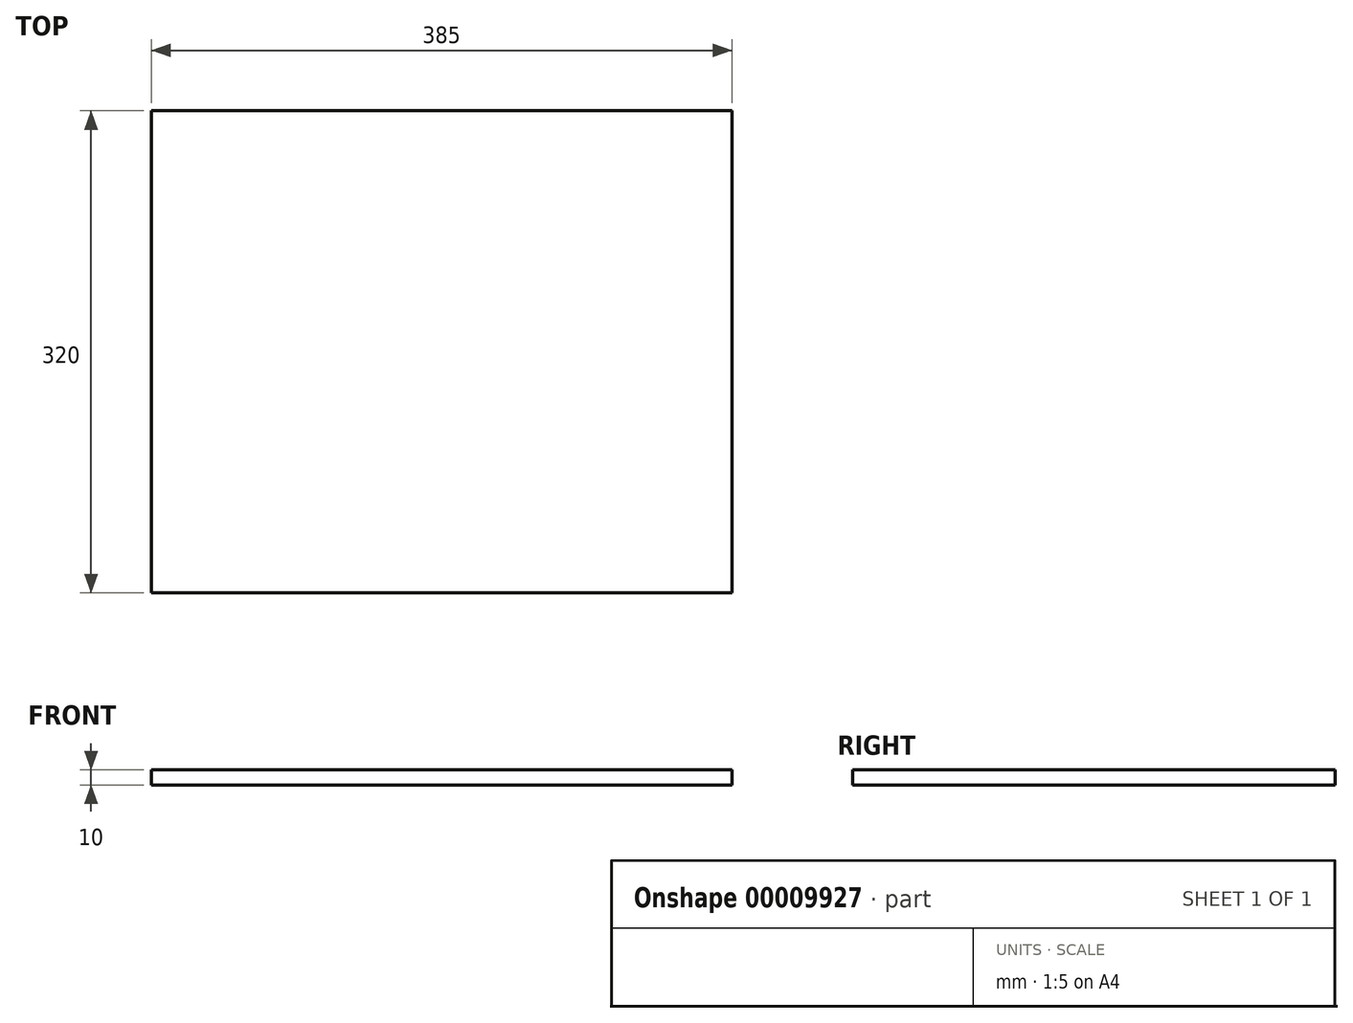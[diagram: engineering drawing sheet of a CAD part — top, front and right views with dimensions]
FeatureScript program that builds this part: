
annotation { "Feature Type Name" : "Feature", "Feature Type Description" : "" }
export const myFeature = defineFeature(function(context is Context, id is Id, definition is map)
    precondition{}
    {
        {
            var Q0;
            Q0=qCreatedBy(makeId("Top.planeOp"),FACE);
            var sketch = newSketch(context, id + "F0", { "sketchPlane" : qUnion([Q0])});
            skLineSegment(sketch, "E0.bottom", {"start": v(-70.96, 65.05) * mm, "end": v(314.04, 65.05) * mm});
            skLineSegment(sketch, "E0.top", {"start": v(-70.96, -254.95) * mm, "end": v(314.04, -254.95) * mm});
            skLineSegment(sketch, "E0.left", {"start": v(-70.96, 65.05) * mm, "end": v(-70.96, -254.95) * mm});
            skLineSegment(sketch, "E0.right", {"start": v(314.04, 65.05) * mm, "end": v(314.04, -254.95) * mm});
            skSolve(sketch);
        }
        {
            var Q0;
            Q0 = qSketchRegion(id + "F0", true);
            extrude(context, id + "F1", {"entities" : qUnion([Q0]), "depth" : 10 * mm});
        }
    });
